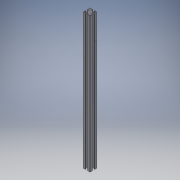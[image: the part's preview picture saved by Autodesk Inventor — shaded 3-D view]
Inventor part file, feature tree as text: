
AUTODESK INVENTOR PART (.ipt)
format: ipt  version: 2019 (Build 230136000, 136)  size: 343,040 bytes
history: native  units: in
note: dims shown in document units (in); Inventor stores cm internally (conversion verified against a paired STEP export)
features: extrude x1, sketch x1, projected_geometry x1
ambient origin geometry x8: Origin, YZ Plane, XZ Plane, XY Plane, X Axis, Y Axis, Z Axis, Center Point
bodies: Solid1 (feature_tree), Body1 (feature_tree)
feature tree (3):
  extrude  "Extrusion1"  [1 undecoded]
  sketch  "Sketch1"  dims[d0=18.1102in d1=0.0in]
  projected_geometry  "Projected Loop1"
note: 1 required parameter value undecoded (feature->parameter linkage not recoverable at this tier; creation-order binding heuristic only, values carry confidence <= 0.55)
